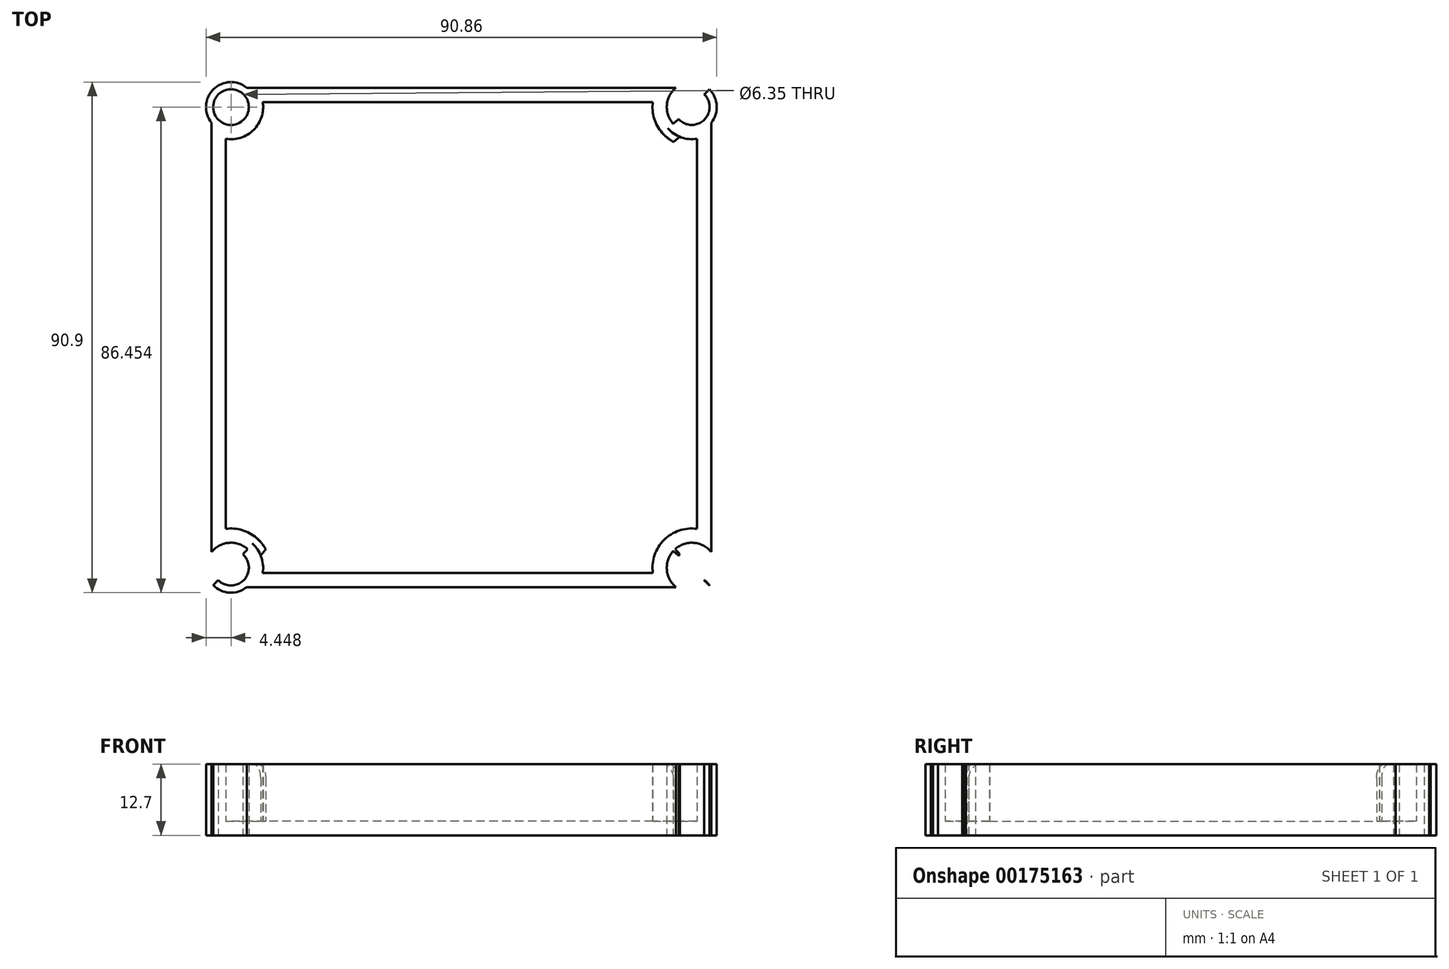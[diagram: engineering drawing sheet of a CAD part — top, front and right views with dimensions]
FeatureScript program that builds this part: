
annotation { "Feature Type Name" : "Feature", "Feature Type Description" : "" }
export const myFeature = defineFeature(function(context is Context, id is Id, definition is map)
    precondition{}
    {
        {
            var Q0;
            Q0=qCreatedBy(makeId("Top.planeOp"),FACE);
            var sketch = newSketch(context, id + "F0", { "sketchPlane" : qUnion([Q0])});
            skLineSegment(sketch, "E0.bottom", {"start": v(44.45, -44.45) * mm, "end": v(-44.45, -44.45) * mm});
            skLineSegment(sketch, "E0.top", {"start": v(44.45, 44.45) * mm, "end": v(-44.45, 44.45) * mm});
            skLineSegment(sketch, "E0.left", {"start": v(44.45, -44.45) * mm, "end": v(44.45, 44.45) * mm});
            skLineSegment(sketch, "E0.right", {"start": v(-44.45, -44.45) * mm, "end": v(-44.45, 44.45) * mm});
            skPoint(sketch, "E0.middle", {"position": v(0, 0) * mm});
            skLineSegment(sketch, "E1.bottom", {"start": v(25.4, -25.4) * mm, "end": v(-25.4, -25.4) * mm});
            skLineSegment(sketch, "E1.top", {"start": v(25.4, 25.4) * mm, "end": v(-25.4, 25.4) * mm});
            skLineSegment(sketch, "E1.left", {"start": v(25.4, -25.4) * mm, "end": v(25.4, 25.4) * mm});
            skLineSegment(sketch, "E1.right", {"start": v(-25.4, -25.4) * mm, "end": v(-25.4, 25.4) * mm});
            skFitSpline(sketch, "E2", {"points": [v(-44.45, 44.45) * mm, v(0, 25.4) * mm, v(44.45, 44.45) * mm], "startDerivative": vector(88.9, -95.25) * mm, "endDerivative": vector(88.9, 95.25) * mm});
            skFitSpline(sketch, "E3", {"points": [v(44.45, 44.45) * mm, v(25.4, 0) * mm, v(44.45, -44.45) * mm], "startDerivative": vector(-95.25, -88.9) * mm, "endDerivative": vector(95.25, -88.9) * mm});
            skFitSpline(sketch, "E4", {"points": [v(44.45, -44.45) * mm, v(0, -25.4) * mm, v(-44.45, -44.45) * mm], "startDerivative": vector(-88.9, 95.25) * mm, "endDerivative": vector(-88.9, -95.25) * mm});
            skFitSpline(sketch, "E5", {"points": [v(-44.45, -44.45) * mm, v(-25.4, 0) * mm, v(-44.45, 44.45) * mm], "startDerivative": vector(95.25, 88.9) * mm, "endDerivative": vector(-95.25, 88.9) * mm});
            skCircle(sketch, "E6", {"center": v(40.98, 41) * mm, "radius": 3.18 * mm});
            skCircle(sketch, "E7", {"center": v(40.98, 41) * mm, "radius": 4.45 * mm});
            skLineSegment(sketch, "E8", {"start": v(0, 25.4) * mm, "end": v(0, 0) * mm});
            skLineSegment(sketch, "E9", {"start": v(25.4, 0) * mm, "end": v(0, 0) * mm});
            skCircle(sketch, "E10.MirrorC", {"center": v(-40.98, 41) * mm, "radius": 4.45 * mm});
            skCircle(sketch, "E11.MirrorC", {"center": v(-40.98, 41) * mm, "radius": 3.18 * mm});
            skCircle(sketch, "E12.MirrorC", {"center": v(40.98, -41) * mm, "radius": 4.45 * mm});
            skCircle(sketch, "E13.MirrorC", {"center": v(40.98, -41) * mm, "radius": 3.18 * mm});
            skCircle(sketch, "E14.MirrorC", {"center": v(-40.98, -41) * mm, "radius": 3.18 * mm});
            skCircle(sketch, "E15.MirrorC", {"center": v(-40.98, -41) * mm, "radius": 4.45 * mm});
            skSolve(sketch);
        }
        {
            var Q0;
            {var subQ0=sQuery(id+"F0.wireOp",EDGE,"E1.right");var subQ1=sQuery(id+"F0.wireOp",EDGE,"E1.top");var subQ2=makeQuery(id+"F0.imprint","INTERSECT",VERTEX,{"derivedFrom":[subQ1,subQ0]});Q0=makeQuery(id+"F0.imprint","IMPRINT",FACE,{"disambiguationData":[TD([[makeQuery(id+"F0.imprint","IMPRINT",EDGE,{"disambiguationData":[TD([[subQ2,1.0]])],"derivedFrom":subQ1}),-1.0]])]});}
            var Q1;
            {var subQ0=sQuery(id+"F0.wireOp",EDGE,"E1.left");var subQ1=sQuery(id+"F0.wireOp",EDGE,"E1.top");var subQ2=makeQuery(id+"F0.imprint","INTERSECT",VERTEX,{"derivedFrom":[subQ1,subQ0]});Q1=makeQuery(id+"F0.imprint","IMPRINT",FACE,{"disambiguationData":[TD([[makeQuery(id+"F0.imprint","IMPRINT",EDGE,{"disambiguationData":[TD([[subQ2,-1.0]])],"derivedFrom":subQ1}),-1.0]])]});}
            var Q2;
            {var subQ4=sQuery(id+"F0.wireOp",EDGE,"E1.left");var subQ6=sQuery(id+"F0.wireOp",EDGE,"E1.bottom");var subQ9=makeQuery(id+"F0.imprint","INTERSECT",VERTEX,{"derivedFrom":[subQ6,subQ4]});Q2=makeQuery(id+"F0.imprint","IMPRINT",FACE,{"disambiguationData":[TD([[makeQuery(id+"F0.imprint","IMPRINT",EDGE,{"disambiguationData":[TD([[subQ9,-1.0]])],"derivedFrom":subQ6}),-1.0]])]});}
            var Q3;
            {var subQ0=sQuery(id+"F0.wireOp",EDGE,"E1.left");var subQ1=sQuery(id+"F0.wireOp",EDGE,"E1.bottom");var subQ2=makeQuery(id+"F0.imprint","INTERSECT",VERTEX,{"derivedFrom":[subQ1,subQ0]});Q3=makeQuery(id+"F0.imprint","IMPRINT",FACE,{"disambiguationData":[TD([[makeQuery(id+"F0.imprint","IMPRINT",EDGE,{"disambiguationData":[TD([[subQ2,-1.0]])],"derivedFrom":subQ1}),1.0]])]});}
            var Q4;
            {var subQ0=sQuery(id+"F0.wireOp",EDGE,"E1.right");var subQ1=sQuery(id+"F0.wireOp",EDGE,"E1.bottom");var subQ2=makeQuery(id+"F0.imprint","INTERSECT",VERTEX,{"derivedFrom":[subQ1,subQ0]});Q4=makeQuery(id+"F0.imprint","IMPRINT",FACE,{"disambiguationData":[TD([[makeQuery(id+"F0.imprint","IMPRINT",EDGE,{"disambiguationData":[TD([[subQ2,1.0]])],"derivedFrom":subQ1}),1.0]])]});}
            var Q5;
            {var subQ3=sQuery(id+"F0.wireOp",EDGE,"E8");Q5=makeQuery(id+"F0.imprint","IMPRINT",FACE,{"disambiguationData":[TD([[makeQuery(id+"F0.imprint","IMPRINT",EDGE,{"derivedFrom":subQ3}),1.0]])]});}
            var Q6;
            {var subQ0=sQuery(id+"F0.wireOp",EDGE,"E7");var subQ1=sQuery(id+"F0.wireOp",EDGE,"E2");var subQ2=makeQuery(id+"F0.imprint","INTERSECT",VERTEX,{"disambiguationData":[OD(0.0)],"derivedFrom":[subQ1,subQ0]});Q6=makeQuery(id+"F0.imprint","IMPRINT",FACE,{"disambiguationData":[TD([[makeQuery(id+"F0.imprint","IMPRINT",EDGE,{"disambiguationData":[TD([[subQ2,-1.0]])],"derivedFrom":subQ1}),-1.0]])]});}
            var Q7;
            {var subQ0=sQuery(id+"F0.wireOp",EDGE,"E11.MirrorC");var subQ1=sQuery(id+"F0.wireOp",EDGE,"E2");var subQ2=makeQuery(id+"F0.imprint","INTERSECT",VERTEX,{"disambiguationData":[OD(1.0)],"derivedFrom":[subQ1,subQ0]});Q7=makeQuery(id+"F0.imprint","IMPRINT",FACE,{"disambiguationData":[TD([[makeQuery(id+"F0.imprint","IMPRINT",EDGE,{"disambiguationData":[TD([[subQ2,-1.0]])],"derivedFrom":subQ1}),-1.0]])]});}
            var Q8;
            {var subQ0=sQuery(id+"F0.wireOp",EDGE,"E15.MirrorC");var subQ1=sQuery(id+"F0.wireOp",EDGE,"E4");var subQ2=makeQuery(id+"F0.imprint","INTERSECT",VERTEX,{"disambiguationData":[OD(0.0)],"derivedFrom":[subQ1,subQ0]});Q8=makeQuery(id+"F0.imprint","IMPRINT",FACE,{"disambiguationData":[TD([[makeQuery(id+"F0.imprint","IMPRINT",EDGE,{"disambiguationData":[TD([[subQ2,-1.0]])],"derivedFrom":subQ1}),-1.0]])]});}
            var Q9;
            {var subQ0=sQuery(id+"F0.wireOp",EDGE,"E12.MirrorC");var subQ1=sQuery(id+"F0.wireOp",EDGE,"E3");var subQ2=makeQuery(id+"F0.imprint","INTERSECT",VERTEX,{"disambiguationData":[OD(0.0)],"derivedFrom":[subQ1,subQ0]});Q9=makeQuery(id+"F0.imprint","IMPRINT",FACE,{"disambiguationData":[TD([[makeQuery(id+"F0.imprint","IMPRINT",EDGE,{"disambiguationData":[TD([[subQ2,-1.0]])],"derivedFrom":subQ1}),-1.0]])]});}
            extrude(context, id + "F1", {"entities" : qUnion([Q0, Q1, Q2, Q3, Q4, Q5, Q6, Q7, Q8, Q9]), "depth" : 12.7 * mm});
        }
        {
            var Q0;
            {var subQ0=sQuery(id+"F0.wireOp",EDGE,"E12.MirrorC");var subQ1=sQuery(id+"F0.wireOp",EDGE,"E0.bottom");var subQ2=makeQuery(id+"F0.imprint","INTERSECT",VERTEX,{"disambiguationData":[OD(0.0)],"derivedFrom":[subQ1,subQ0]});Q0=makeQuery(id+"F0.imprint","IMPRINT",FACE,{"disambiguationData":[TD([[makeQuery(id+"F0.imprint","IMPRINT",EDGE,{"disambiguationData":[TD([[subQ2,-1.0]])],"derivedFrom":subQ1}),-1.0]])]});}
            var Q1;
            {var subQ0=sQuery(id+"F0.wireOp",EDGE,"E12.MirrorC");var subQ1=sQuery(id+"F0.wireOp",EDGE,"E0.bottom");var subQ2=makeQuery(id+"F0.imprint","INTERSECT",VERTEX,{"disambiguationData":[OD(0.0)],"derivedFrom":[subQ1,subQ0]});Q1=makeQuery(id+"F0.imprint","IMPRINT",FACE,{"disambiguationData":[TD([[makeQuery(id+"F0.imprint","IMPRINT",EDGE,{"disambiguationData":[TD([[subQ2,-1.0]])],"derivedFrom":subQ1}),1.0]])]});}
            var Q2;
            {var subQ0=sQuery(id+"F0.wireOp",EDGE,"E12.MirrorC");var subQ1=sQuery(id+"F0.wireOp",EDGE,"E0.left");var subQ2=makeQuery(id+"F0.imprint","INTERSECT",VERTEX,{"disambiguationData":[OD(0.0)],"derivedFrom":[subQ1,subQ0]});Q2=makeQuery(id+"F0.imprint","IMPRINT",FACE,{"disambiguationData":[TD([[makeQuery(id+"F0.imprint","IMPRINT",EDGE,{"disambiguationData":[TD([[subQ2,-1.0]])],"derivedFrom":subQ1}),-1.0]])]});}
            var Q3;
            {var subQ0=sQuery(id+"F0.wireOp",EDGE,"E12.MirrorC");var subQ1=sQuery(id+"F0.wireOp",EDGE,"E0.left");var subQ2=makeQuery(id+"F0.imprint","INTERSECT",VERTEX,{"disambiguationData":[OD(0.0)],"derivedFrom":[subQ1,subQ0]});Q3=makeQuery(id+"F0.imprint","IMPRINT",FACE,{"disambiguationData":[TD([[makeQuery(id+"F0.imprint","IMPRINT",EDGE,{"disambiguationData":[TD([[subQ2,-1.0]])],"derivedFrom":subQ1}),1.0]])]});}
            var Q4;
            {var subQ0=sQuery(id+"F0.wireOp",EDGE,"E12.MirrorC");var subQ1=sQuery(id+"F0.wireOp",EDGE,"E3");var subQ2=makeQuery(id+"F0.imprint","INTERSECT",VERTEX,{"disambiguationData":[OD(0.0)],"derivedFrom":[subQ1,subQ0]});Q4=makeQuery(id+"F0.imprint","IMPRINT",FACE,{"disambiguationData":[TD([[makeQuery(id+"F0.imprint","IMPRINT",EDGE,{"disambiguationData":[TD([[subQ2,-1.0]])],"derivedFrom":subQ1}),-1.0]])]});}
            var Q5;
            {var subQ0=sQuery(id+"F0.wireOp",EDGE,"E15.MirrorC");var subQ8=sQuery(id+"F0.wireOp",EDGE,"E0.bottom");var subQ9=makeQuery(id+"F0.imprint","INTERSECT",VERTEX,{"disambiguationData":[OD(0.0)],"derivedFrom":[subQ8,subQ0]});Q5=makeQuery(id+"F0.imprint","IMPRINT",FACE,{"disambiguationData":[TD([[makeQuery(id+"F0.imprint","IMPRINT",EDGE,{"disambiguationData":[TD([[subQ9,-1.0]])],"derivedFrom":subQ8}),-1.0]])]});}
            var Q6;
            {var subQ0=sQuery(id+"F0.wireOp",EDGE,"E15.MirrorC");var subQ1=sQuery(id+"F0.wireOp",EDGE,"E0.bottom");var subQ2=makeQuery(id+"F0.imprint","INTERSECT",VERTEX,{"disambiguationData":[OD(0.0)],"derivedFrom":[subQ1,subQ0]});Q6=makeQuery(id+"F0.imprint","IMPRINT",FACE,{"disambiguationData":[TD([[makeQuery(id+"F0.imprint","IMPRINT",EDGE,{"disambiguationData":[TD([[subQ2,-1.0]])],"derivedFrom":subQ1}),1.0]])]});}
            var Q7;
            {var subQ0=sQuery(id+"F0.wireOp",EDGE,"E15.MirrorC");var subQ1=sQuery(id+"F0.wireOp",EDGE,"E0.right");var subQ2=makeQuery(id+"F0.imprint","INTERSECT",VERTEX,{"disambiguationData":[OD(0.0)],"derivedFrom":[subQ1,subQ0]});Q7=makeQuery(id+"F0.imprint","IMPRINT",FACE,{"disambiguationData":[TD([[makeQuery(id+"F0.imprint","IMPRINT",EDGE,{"disambiguationData":[TD([[subQ2,-1.0]])],"derivedFrom":subQ1}),1.0]])]});}
            var Q8;
            {var subQ5=sQuery(id+"F0.wireOp",EDGE,"E15.MirrorC");var subQ7=sQuery(id+"F0.wireOp",EDGE,"E0.right");var subQ10=makeQuery(id+"F0.imprint","INTERSECT",VERTEX,{"disambiguationData":[OD(0.0)],"derivedFrom":[subQ7,subQ5]});Q8=makeQuery(id+"F0.imprint","IMPRINT",FACE,{"disambiguationData":[TD([[makeQuery(id+"F0.imprint","IMPRINT",EDGE,{"disambiguationData":[TD([[subQ10,-1.0]])],"derivedFrom":subQ7}),-1.0]])]});}
            var Q9;
            {var subQ0=sQuery(id+"F0.wireOp",EDGE,"E15.MirrorC");var subQ1=sQuery(id+"F0.wireOp",EDGE,"E4");var subQ2=makeQuery(id+"F0.imprint","INTERSECT",VERTEX,{"disambiguationData":[OD(0.0)],"derivedFrom":[subQ1,subQ0]});Q9=makeQuery(id+"F0.imprint","IMPRINT",FACE,{"disambiguationData":[TD([[makeQuery(id+"F0.imprint","IMPRINT",EDGE,{"disambiguationData":[TD([[subQ2,-1.0]])],"derivedFrom":subQ1}),-1.0]])]});}
            var Q10;
            {var subQ0=sQuery(id+"F0.wireOp",EDGE,"E10.MirrorC");var subQ1=sQuery(id+"F0.wireOp",EDGE,"E0.top");var subQ2=makeQuery(id+"F0.imprint","INTERSECT",VERTEX,{"disambiguationData":[OD(0.0)],"derivedFrom":[subQ1,subQ0]});Q10=makeQuery(id+"F0.imprint","IMPRINT",FACE,{"disambiguationData":[TD([[makeQuery(id+"F0.imprint","IMPRINT",EDGE,{"disambiguationData":[TD([[subQ2,-1.0]])],"derivedFrom":subQ1}),-1.0]])]});}
            var Q11;
            {var subQ0=sQuery(id+"F0.wireOp",EDGE,"E10.MirrorC");var subQ1=sQuery(id+"F0.wireOp",EDGE,"E0.right");var subQ2=makeQuery(id+"F0.imprint","INTERSECT",VERTEX,{"disambiguationData":[OD(0.0)],"derivedFrom":[subQ1,subQ0]});Q11=makeQuery(id+"F0.imprint","IMPRINT",FACE,{"disambiguationData":[TD([[makeQuery(id+"F0.imprint","IMPRINT",EDGE,{"disambiguationData":[TD([[subQ2,-1.0]])],"derivedFrom":subQ1}),1.0]])]});}
            var Q12;
            {var subQ0=sQuery(id+"F0.wireOp",EDGE,"E10.MirrorC");var subQ1=sQuery(id+"F0.wireOp",EDGE,"E0.right");var subQ10=makeQuery(id+"F0.imprint","INTERSECT",VERTEX,{"disambiguationData":[OD(0.0)],"derivedFrom":[subQ1,subQ0]});Q12=makeQuery(id+"F0.imprint","IMPRINT",FACE,{"disambiguationData":[TD([[makeQuery(id+"F0.imprint","IMPRINT",EDGE,{"disambiguationData":[TD([[subQ10,-1.0]])],"derivedFrom":subQ1}),-1.0]])]});}
            var Q13;
            {var subQ0=sQuery(id+"F0.wireOp",EDGE,"E10.MirrorC");var subQ1=sQuery(id+"F0.wireOp",EDGE,"E0.top");var subQ10=makeQuery(id+"F0.imprint","INTERSECT",VERTEX,{"disambiguationData":[OD(0.0)],"derivedFrom":[subQ1,subQ0]});Q13=makeQuery(id+"F0.imprint","IMPRINT",FACE,{"disambiguationData":[TD([[makeQuery(id+"F0.imprint","IMPRINT",EDGE,{"disambiguationData":[TD([[subQ10,-1.0]])],"derivedFrom":subQ1}),1.0]])]});}
            var Q14;
            {var subQ0=sQuery(id+"F0.wireOp",EDGE,"E11.MirrorC");var subQ1=sQuery(id+"F0.wireOp",EDGE,"E2");var subQ2=makeQuery(id+"F0.imprint","INTERSECT",VERTEX,{"disambiguationData":[OD(1.0)],"derivedFrom":[subQ1,subQ0]});Q14=makeQuery(id+"F0.imprint","IMPRINT",FACE,{"disambiguationData":[TD([[makeQuery(id+"F0.imprint","IMPRINT",EDGE,{"disambiguationData":[TD([[subQ2,-1.0]])],"derivedFrom":subQ1}),-1.0]])]});}
            var Q15;
            {var subQ0=sQuery(id+"F0.wireOp",EDGE,"E10.MirrorC");var subQ1=sQuery(id+"F0.wireOp",EDGE,"E2");var subQ2=makeQuery(id+"F0.imprint","INTERSECT",VERTEX,{"disambiguationData":[OD(0.0)],"derivedFrom":[subQ1,subQ0]});Q15=makeQuery(id+"F0.imprint","IMPRINT",FACE,{"disambiguationData":[TD([[makeQuery(id+"F0.imprint","IMPRINT",EDGE,{"disambiguationData":[TD([[subQ2,-1.0]])],"derivedFrom":subQ1}),1.0]])]});}
            var Q16;
            {var subQ0=sQuery(id+"F0.wireOp",EDGE,"E14.MirrorC");var subQ1=sQuery(id+"F0.wireOp",EDGE,"E4");var subQ2=makeQuery(id+"F0.imprint","INTERSECT",VERTEX,{"disambiguationData":[OD(1.0)],"derivedFrom":[subQ1,subQ0]});Q16=makeQuery(id+"F0.imprint","IMPRINT",FACE,{"disambiguationData":[TD([[makeQuery(id+"F0.imprint","IMPRINT",EDGE,{"disambiguationData":[TD([[subQ2,-1.0]])],"derivedFrom":subQ1}),1.0]])]});}
            var Q17;
            {var subQ0=sQuery(id+"F0.wireOp",EDGE,"E13.MirrorC");var subQ1=sQuery(id+"F0.wireOp",EDGE,"E3");var subQ2=makeQuery(id+"F0.imprint","INTERSECT",VERTEX,{"disambiguationData":[OD(1.0)],"derivedFrom":[subQ1,subQ0]});Q17=makeQuery(id+"F0.imprint","IMPRINT",FACE,{"disambiguationData":[TD([[makeQuery(id+"F0.imprint","IMPRINT",EDGE,{"disambiguationData":[TD([[subQ2,-1.0]])],"derivedFrom":subQ1}),1.0]])]});}
            var Q18;
            {var subQ0=sQuery(id+"F0.wireOp",EDGE,"E7");var subQ1=sQuery(id+"F0.wireOp",EDGE,"E2");var subQ2=makeQuery(id+"F0.imprint","INTERSECT",VERTEX,{"disambiguationData":[OD(0.0)],"derivedFrom":[subQ1,subQ0]});Q18=makeQuery(id+"F0.imprint","IMPRINT",FACE,{"disambiguationData":[TD([[makeQuery(id+"F0.imprint","IMPRINT",EDGE,{"disambiguationData":[TD([[subQ2,-1.0]])],"derivedFrom":subQ1}),-1.0]])]});}
            var Q19;
            {var subQ5=sQuery(id+"F0.wireOp",EDGE,"E7");var subQ6=sQuery(id+"F0.wireOp",EDGE,"E0.top");var subQ10=makeQuery(id+"F0.imprint","INTERSECT",VERTEX,{"disambiguationData":[OD(0.0)],"derivedFrom":[subQ6,subQ5]});Q19=makeQuery(id+"F0.imprint","IMPRINT",FACE,{"disambiguationData":[TD([[makeQuery(id+"F0.imprint","IMPRINT",EDGE,{"disambiguationData":[TD([[subQ10,-1.0]])],"derivedFrom":subQ6}),1.0]])]});}
            var Q20;
            {var subQ5=sQuery(id+"F0.wireOp",EDGE,"E7");var subQ6=sQuery(id+"F0.wireOp",EDGE,"E0.left");var subQ7=makeQuery(id+"F0.imprint","INTERSECT",VERTEX,{"disambiguationData":[OD(0.0)],"derivedFrom":[subQ6,subQ5]});Q20=makeQuery(id+"F0.imprint","IMPRINT",FACE,{"disambiguationData":[TD([[makeQuery(id+"F0.imprint","IMPRINT",EDGE,{"disambiguationData":[TD([[subQ7,-1.0]])],"derivedFrom":subQ6}),1.0]])]});}
            var Q21;
            {var subQ0=sQuery(id+"F0.wireOp",EDGE,"E7");var subQ1=sQuery(id+"F0.wireOp",EDGE,"E0.left");var subQ2=makeQuery(id+"F0.imprint","INTERSECT",VERTEX,{"disambiguationData":[OD(0.0)],"derivedFrom":[subQ1,subQ0]});Q21=makeQuery(id+"F0.imprint","IMPRINT",FACE,{"disambiguationData":[TD([[makeQuery(id+"F0.imprint","IMPRINT",EDGE,{"disambiguationData":[TD([[subQ2,-1.0]])],"derivedFrom":subQ1}),-1.0]])]});}
            var Q22;
            {var subQ0=sQuery(id+"F0.wireOp",EDGE,"E7");var subQ1=sQuery(id+"F0.wireOp",EDGE,"E0.top");var subQ2=makeQuery(id+"F0.imprint","INTERSECT",VERTEX,{"disambiguationData":[OD(0.0)],"derivedFrom":[subQ1,subQ0]});Q22=makeQuery(id+"F0.imprint","IMPRINT",FACE,{"disambiguationData":[TD([[makeQuery(id+"F0.imprint","IMPRINT",EDGE,{"disambiguationData":[TD([[subQ2,-1.0]])],"derivedFrom":subQ1}),-1.0]])]});}
            var Q23;
            {var subQ0=sQuery(id+"F0.wireOp",EDGE,"E6");var subQ1=sQuery(id+"F0.wireOp",EDGE,"E2");var subQ2=makeQuery(id+"F0.imprint","INTERSECT",VERTEX,{"disambiguationData":[OD(1.0)],"derivedFrom":[subQ1,subQ0]});Q23=makeQuery(id+"F0.imprint","IMPRINT",FACE,{"disambiguationData":[TD([[makeQuery(id+"F0.imprint","IMPRINT",EDGE,{"disambiguationData":[TD([[subQ2,-1.0]])],"derivedFrom":subQ1}),1.0]])]});}
            extrude(context, id + "F2", {"entities" : qUnion([Q0, Q1, Q2, Q3, Q4, Q5, Q6, Q7, Q8, Q9, Q10, Q11, Q12, Q13, Q14, Q15, Q16, Q17, Q18, Q19, Q20, Q21, Q22, Q23]), "depth" : 12.7 * mm});
        }
        {
            var Q0;
            Q0=makeQuery(id+"F1.opExtrude","SWEPT_BODY",BODY,{"disambiguationData":[OSD([sQuery(id+"F0.wireOp",EDGE,"E2"),sQuery(id+"F0.wireOp",EDGE,"E3"),sQuery(id+"F0.wireOp",EDGE,"E4"),sQuery(id+"F0.wireOp",EDGE,"E5"),sQuery(id+"F0.wireOp",EDGE,"E6"),sQuery(id+"F0.wireOp",EDGE,"E11.MirrorC"),sQuery(id+"F0.wireOp",EDGE,"E13.MirrorC"),sQuery(id+"F0.wireOp",EDGE,"E14.MirrorC")])]});
            var Q1;
            Q1=makeQuery(id+"F2.opExtrude","SWEPT_BODY",BODY,{"disambiguationData":[OSD([sQuery(id+"F0.wireOp",EDGE,"E6"),sQuery(id+"F0.wireOp",EDGE,"E7")])]});
            var Q2;
            Q2=makeQuery(id+"F2.opExtrude","SWEPT_BODY",BODY,{"disambiguationData":[OSD([sQuery(id+"F0.wireOp",EDGE,"E10.MirrorC"),sQuery(id+"F0.wireOp",EDGE,"E11.MirrorC")])]});
            var Q3;
            Q3=makeQuery(id+"F2.opExtrude","SWEPT_BODY",BODY,{"disambiguationData":[OSD([sQuery(id+"F0.wireOp",EDGE,"E12.MirrorC"),sQuery(id+"F0.wireOp",EDGE,"E13.MirrorC")])]});
            var Q4;
            Q4=makeQuery(id+"F2.opExtrude","SWEPT_BODY",BODY,{"disambiguationData":[OSD([sQuery(id+"F0.wireOp",EDGE,"E14.MirrorC"),sQuery(id+"F0.wireOp",EDGE,"E15.MirrorC")])]});
            booleanBodies(context, id + "F3", {"operationType" : BooleanOperationType.UNION, "tools" : qUnion([Q0, Q1, Q2, Q3, Q4])});
        }
        {
            var Q0;
            {var subQ0=sQuery(id+"F0.wireOp",EDGE,"E14.MirrorC");var subQ1=sQuery(id+"F0.wireOp",EDGE,"E13.MirrorC");var subQ2=sQuery(id+"F0.wireOp",EDGE,"E11.MirrorC");var subQ3=sQuery(id+"F0.wireOp",EDGE,"E6");Q0=makeQuery(id+"F3.opBoolean","MERGE",FACE,{"derivedFrom":[makeQuery(id+"F1.opExtrude","CAP_FACE",FACE,{"disambiguationData":[OSD([sQuery(id+"F0.wireOp",EDGE,"E2"),sQuery(id+"F0.wireOp",EDGE,"E3"),sQuery(id+"F0.wireOp",EDGE,"E4"),sQuery(id+"F0.wireOp",EDGE,"E5"),subQ3,subQ2,subQ1,subQ0])],"isStart":false}),makeQuery(id+"F2.opExtrude","CAP_FACE",FACE,{"disambiguationData":[OSD([subQ3,sQuery(id+"F0.wireOp",EDGE,"E7")])],"isStart":false}),makeQuery(id+"F2.opExtrude","CAP_FACE",FACE,{"disambiguationData":[OSD([sQuery(id+"F0.wireOp",EDGE,"E10.MirrorC"),subQ2])],"isStart":false}),makeQuery(id+"F2.opExtrude","CAP_FACE",FACE,{"disambiguationData":[OSD([sQuery(id+"F0.wireOp",EDGE,"E12.MirrorC"),subQ1])],"isStart":false}),makeQuery(id+"F2.opExtrude","CAP_FACE",FACE,{"disambiguationData":[OSD([subQ0,sQuery(id+"F0.wireOp",EDGE,"E15.MirrorC")])],"isStart":false})]});}
            shell(context, id + "F4", {"entities" : qUnion([Q0]), "thickness" : 2.54 * mm});
        }
        {
            var Q0;
            {var subQ0=sQuery(id+"F0.wireOp",EDGE,"E2");Q0=makeQuery(id+"F4.opShell","OFFSET_EDGE",EDGE,{"disambiguationData":[OSD([subQ0]),TDD([makeQuery(id+"F1.opExtrude","CAP_EDGE",EDGE,{"disambiguationData":[OSD([subQ0])],"isStart":false})])]});}
            var Q1;
            {var subQ0=sQuery(id+"F0.wireOp",EDGE,"E5");Q1=makeQuery(id+"F4.opShell","OFFSET_EDGE",EDGE,{"disambiguationData":[OSD([subQ0]),TDD([makeQuery(id+"F1.opExtrude","CAP_EDGE",EDGE,{"disambiguationData":[OSD([subQ0])],"isStart":false})])]});}
            var Q2;
            {var subQ0=sQuery(id+"F0.wireOp",EDGE,"E3");Q2=makeQuery(id+"F4.opShell","OFFSET_EDGE",EDGE,{"disambiguationData":[OSD([subQ0]),TDD([makeQuery(id+"F1.opExtrude","CAP_EDGE",EDGE,{"disambiguationData":[OSD([subQ0])],"isStart":false})])]});}
            var Q3;
            {var subQ0=sQuery(id+"F0.wireOp",EDGE,"E4");Q3=makeQuery(id+"F4.opShell","OFFSET_EDGE",EDGE,{"disambiguationData":[OSD([subQ0]),TDD([makeQuery(id+"F1.opExtrude","CAP_EDGE",EDGE,{"disambiguationData":[OSD([subQ0])],"isStart":false})])]});}
            fillet(context, id + "F5", {"entities" : qUnion([Q0, Q1, Q2, Q3]), "radius" : 2.54 * mm, "tangentPropagation" : true, "allowEdgeOverflow" : false});
        }
    });
